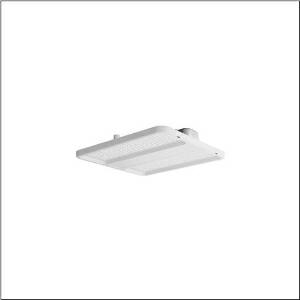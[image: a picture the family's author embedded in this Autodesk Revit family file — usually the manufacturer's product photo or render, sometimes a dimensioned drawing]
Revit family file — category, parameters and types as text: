
# Revit family: highbay_11_midi_51hn12da4fda
name_source: partatom
category: Lighting Fixtures
units: mm (PartAtom-declared; Revit-internal decimal feet)

## family parameters
Cut with Voids When Loaded = No
Host = Face
Light Source = No
Part Type = Normal
Room Calculation Point = No
Round Connector Dimension = Use Diameter
Shared = No

## types (1)
- --- (1 x LED, 2310 lm, 11.8 W, 4000K)
    Apparent Load = 12 VA
    CIE Flux Codes = 87 98 100 100 100
    Color Rendering = 80
    Color Temperature = 4000K
    Default Elevation = 1800 mm
    Description = high bay luminaire Highbay 11 midi; direct symmetric wide distribution, light control with lens of PMMA; UGR ≤ 22 (X = 4H | Y = 8H | S = 0.25H | reflection values 70/50/20); luminous flux: 15.000lm; light colour: 840, colour temperature: 4000K, MacAdam ≤ 2 SDCM (initial), colour rendering: CRI > 80; luminous efficacy: 204,9lm/W; rated service life: 100.000h (L95/B50) at AT= 25°C; control: DALI 2; housing frame of high-performance plastic PA6, matt traffic white (RAL 9016); cover of PMMA; dimension (LxWxH): 474 x 442 x 72mm; luminaire connection: terminal, 5-pole, max. 2.5mm² (cable entry for one cable, Ø 8.5..16mm); mains connection: 230..240V, AC/DC 0/50..60Hz; connected load: 73,2W; protection rating (complete): IP66; insulation class (complete): insulation class I (protective earthing); protection symbol: D; impact resistance: IK08; halogen-free wiring; for central battery installations according to DIN EN 60598-2-22; corresponds to IFS (International Featured Standards) requirements for safety and quality in the food industry; LABS conformity tested according to VDMA 24364:2018-05; certification: CE, ENEC, VDE, UKCA; permissible operating ambient temperature: -40..+65°C (reducing of maximum allowable ambient temperature of 5°C with ceiling mounting); packaging unit: 1 piece; (delivery without accessories; please order mounting accessories separately)
    Height = 72 mm  [stored 0.23622 ft]
    Lamp = 1 x LED
    Lamp Light Flux = 2310 lm
    Lamp Power = 11.8 W
    Lamp count = 1
    Length = 474 mm
    Luminous efficacy = 196 lm/W
    Manufacturer = Siteco
    ModVariant = No
    Model = 51HN12DA4FDA
    Mounting Place = Ceiling
    Mounting Type = Pendant
    Number of Poles = 1
    OnlyDefault = Yes
    Power Factor = 1
    Product Name = Highbay 11 midi
    Product group = high bay luminaire
    ProductGroupID = 901
    Protection Class = Protection class I
    Protection Degree = IP 66
    RLX_Detail_Level = 1
    RLX_Emergency_Light_Flux = 0 lm
    RLX_Emergency_Type = 0
    RLX_Emergency_Type_DB = No
    RlxData = <blob elided: 16669 chars, md5=348c2003>
    Socket = socket
    Standby Power = 0 W
    System Light Flux = 2310 lm
    System Power = 12 W
    Type Comments = : DC mode (central or group accumulator) initial emergency light level
    Type Image = l_1363240.jpg
    URL = http://relux.com
    VarID = @adj_005185
    Voltage = 0 V
    Weight = 0.00 kg
    Width = 442 mm

note: [stored X ft] marks values corroborated as IEEE doubles in the binary element streams (Revit-internal decimal feet)

## geometry (parser evidence)
native form markers: Blend x4, Sweep x10
no freeform markers — native parametric forms only
